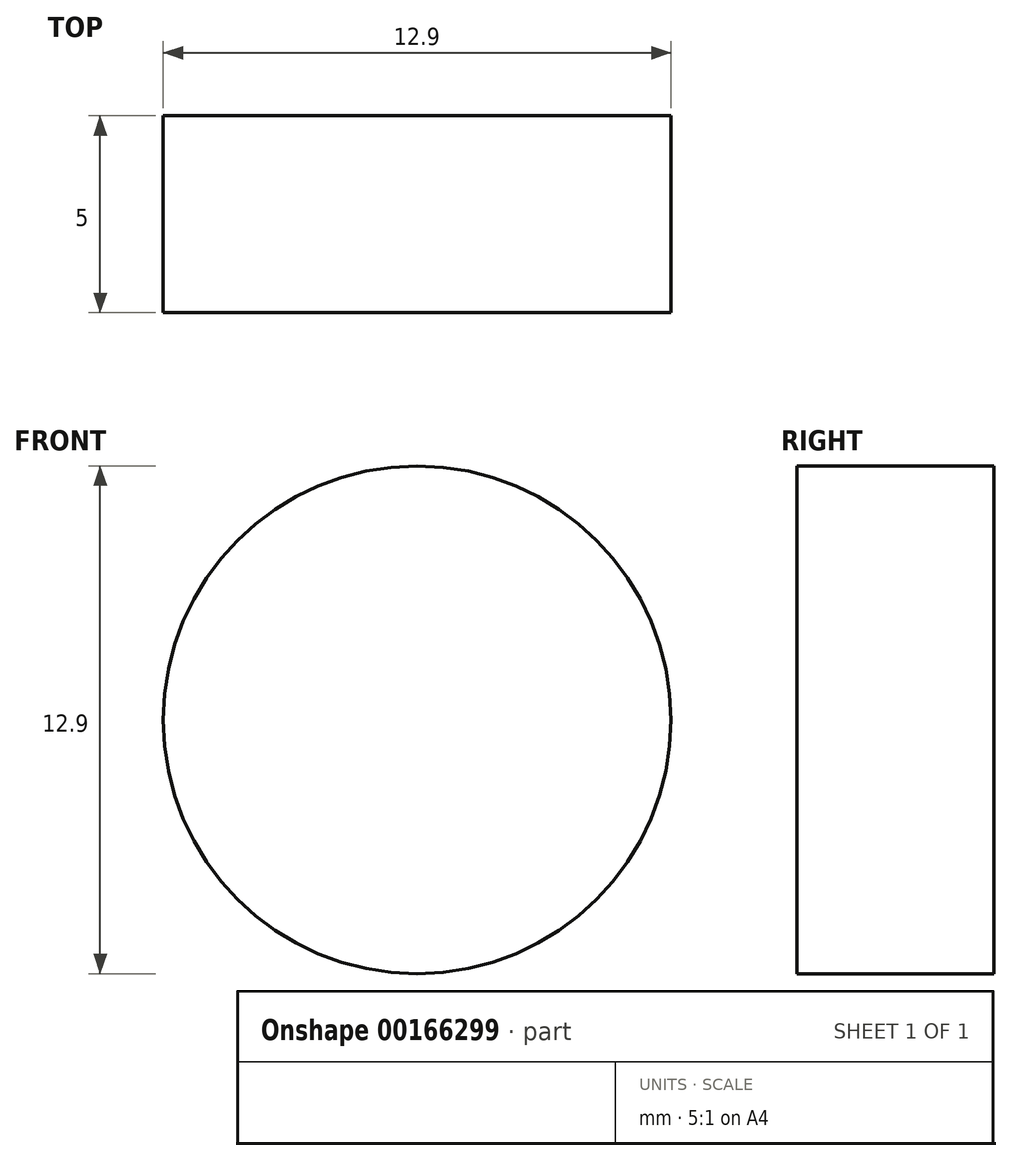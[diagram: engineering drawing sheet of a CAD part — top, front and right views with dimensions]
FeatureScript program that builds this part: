
annotation { "Feature Type Name" : "Feature", "Feature Type Description" : "" }
export const myFeature = defineFeature(function(context is Context, id is Id, definition is map)
    precondition{}
    {
        {
            assignVariable(context, id + "F0", {"name" : "Main_Length", "anyValue" : 5});
        }
        {
            var Q0;
            Q0=qCreatedBy(makeId("Front.planeOp"),FACE);
            var sketch = newSketch(context, id + "F1", { "sketchPlane" : qUnion([Q0])});
            skCircle(sketch, "E0", {"center": v(0, 0) * mm, "radius": 6.45 * mm});
            skSolve(sketch);
        }
        {
            var Q0;
            Q0=makeQuery(id+"F1.imprint","IMPRINT",FACE,{"disambiguationData":[TD([[makeQuery(id+"F1.imprint","IMPRINT",EDGE,{"derivedFrom":sQuery(id+"F1.wireOp",EDGE,"E0")}),1.0]])]});
            extrude(context, id + "F2", {"entities" : qUnion([Q0]), "depth" : (getVariable(context, 'Main_Length')) * mm});
        }
    });
